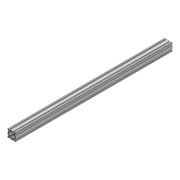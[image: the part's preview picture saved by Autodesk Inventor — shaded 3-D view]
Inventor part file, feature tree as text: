
AUTODESK INVENTOR PART (.ipt)
format: ipt  version: 2018 (Build 220112000, 112)  size: 299,008 bytes
history: native  units: mm
features: extrude x1, sketch x1
ambient origin geometry x8: Origin, YZ Plane, XZ Plane, XY Plane, X Axis, Y Axis, Z Axis, Center Point
bodies: Solid1 (feature_tree)
feature tree (2):
  extrude  "Extrusion1"  [1 undecoded]
  sketch  "Sketch1"  dims[d0=800.0mm d1=0.0mm]
note: 1 required parameter value undecoded (feature->parameter linkage not recoverable at this tier; creation-order binding heuristic only, values carry confidence <= 0.55)
